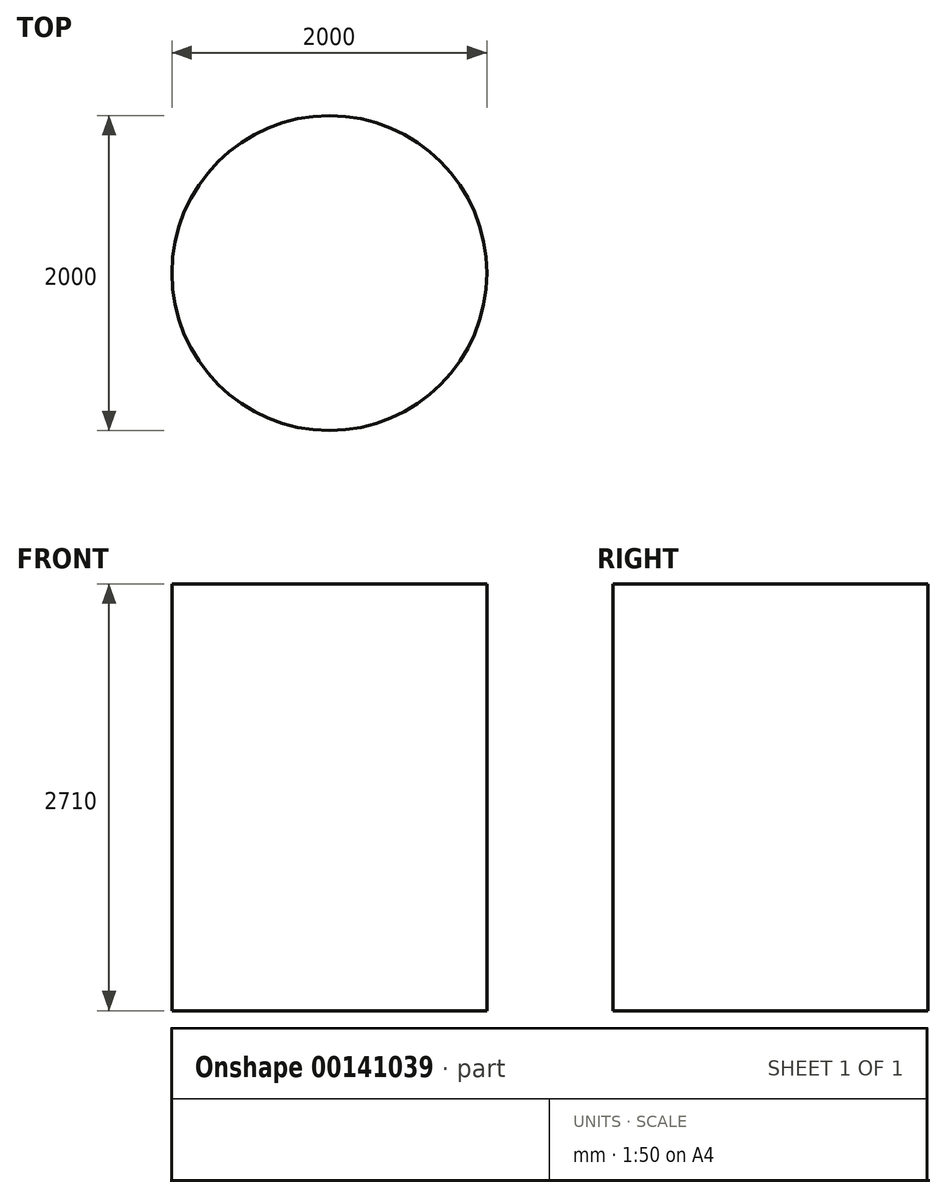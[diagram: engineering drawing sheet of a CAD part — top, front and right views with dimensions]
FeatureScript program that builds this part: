
annotation { "Feature Type Name" : "Feature", "Feature Type Description" : "" }
export const myFeature = defineFeature(function(context is Context, id is Id, definition is map)
    precondition{}
    {
        {
            var Q0;
            Q0=qCreatedBy(makeId("Top.planeOp"),FACE);
            var sketch = newSketch(context, id + "F0", { "sketchPlane" : qUnion([Q0])});
            skCircle(sketch, "E0", {"center": v(0, 0) * mm, "radius": 1000 * mm});
            skSolve(sketch);
        }
        {
            var Q0;
            Q0=qSketchRegion(id+"F0",true);
            extrude(context, id + "F1", {"entities" : qUnion([Q0]), "depth" : 2710 * mm});
        }
    });
